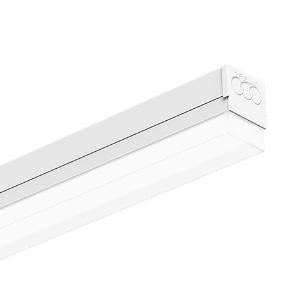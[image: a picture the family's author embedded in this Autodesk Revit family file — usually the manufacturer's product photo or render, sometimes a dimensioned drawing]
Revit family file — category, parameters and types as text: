
# Revit family: 3f_filippi_-_3f_zeta_dr_3f_filippi_-_10971_-_3f_zeta_dr_2x18_led_dali_l1194
name_source: partatom
category: Lighting Fixtures
units: mm (PartAtom-declared; Revit-internal decimal feet)

## family parameters
Cut with Voids When Loaded = No
Host = Face
Light Source = No
Part Type = Normal
Room Calculation Point = No
Round Connector Dimension = Use Diameter
Shared = No

## types (1)
- 3F Filippi - 3F Zeta DR (1 x LED, 4851 lm, 40 W, 4000 K)
    Apparent Load = 40 VA
    Approval mark = CE
    CIE Flux Codes = 41 72 91 86 100
    Color Rendering = 80
    Color Temperature = 4000 K
    Control Gear = Electronic transformer
    Default Elevation = 1800 mm
    Description = ILLUMINOTECHNICAL
Luminous efficiency 100% (DLOR 86%, ULOR 14%).
Initial luminous flux of the luminaire 4851 lm.
Diffused symmetric distribution.
Installation Interdistance Transv.D = 1.31 x hu - Long.D = 1.25 x hu.
Tabular UGR (CIE 117 - 4H-8H; S=0.25H; 70/50/20): RUG 25.5 - 24.1.
Beam angle: 136° - 112°.
Luminous efficacy 121 lm/W.
Lifetime (L93/B10): 30000 h. (tq+25°C)
Lifetime (L90/B10): 50000 h. (tq+25°C)
Lifetime (L85/B10): 80000 h. (tq+25°C)
Lifetime (L80/B10): 100000 h. (tq+25°C)
Sudden decreased luminous flux after 50000 hours: 0% (C0).
Photobiological safety in compliance with IEC/TR 62778: RG0 risk exempt, (IEC 62471).
In compliance with IEC/EN 62722-2-1 - IEC/EN 62717 standards.

SOURCE
2 linear LED modules 18W/840.
Energy efficiency class (UE 2019/2020 - UE 2019/2015): D.
CIE 13.3 Colour rendering index: CRI >80 (R9 <50%).
IES TM-30 Fidelity Index: Rf = 84 Rg = 95.
CCT nominal colour temperature 4000 K.
Colour initial tolerance (MacAdam): SDCM 3.

MECHANICAL
Housing in hot-galvanised steel, painted in white polyester, obtained through rolling process.
Light unit in hot-galvanised steel, painted in white polyester base with fixing springs and retractable safety hooks in stainless steel.
Rectangular screen in self-extinguishing polycarbonate, UV stabilised, opal, with smooth outer surface.
End caps in white polycarbonate.
Pair of stainless steel sliding brackets with sliding block screws.
Luminaire with limited surface temperature. - D - (EN 60598-2-24)
Dimensions: 1194x62 mm, height 81 mm. Weight 3.5 kg.
IP40 protection degree.
Mechanical strength to impacts IK06 (1 joule).
Glow-wire test resistance 850°C.

ELECTRICAL
Halogen Free DALI-2 DATI (Parts 251, 252, 253), PUSH-DIM, electronic wiring 230V-50/60Hz, power factor 0.95 at full load, THD <25%, constant output current, SELV, class I, 1 driver, 1 DALI addresse.
Power of the luminaire 40 W.
ENEC - CE.
SAFE FLICKER: PstLM=<1 and SVM=<0.4 (IEC TR 61547-1 and IEC TR 63158), to ensure a more comfortable and safe light.
Luminaire compliant with EN 60598-2-22 for power supply from a centralised emergency system CPSS (Central Power Supply System), not incorporated in the luminaire - high risk areas excluded. The default power and flux are 100% in AC and 15% in DC.
Ambient temperature from 0°C to +25°C.
Temperature class T6 max 85°C.
Relative humidity UR: <85%.

INSTALLATION
Ceiling / Suspended / Wall.
All accessories dedicated to this product are available on the Catalog and on our website www.3F-Filippi.com.

APPLICATIONS
Suitable product for food production plants (HACCP), IFS (Food Version 6), BRC (GSFS Food Version 7).
In commercial environments, exhibition areas, shops and stores.

LIGHT MANAGEMENT
Recommended minimum setting: 10%.
The luminaire, equipped with (DALI-2 DATI) driver, can be controlled manually with 3F Easy Dim technology or automatically/manually with wired or wireless DALI/D2D control systems.
The D2D driver guarantees interoperability with other devices with the same certification by making the following information available:
Device Data (Part 251), Energy Report (Part 252), Diagnosis & Maintenance (Part 253).
In electrical systems without a regulation system (manual or automatic) and DALI bus, a suitable jumper must be made on the DA-DA terminals of the appliance.

WARNING
Luminaire designed for disposal/recycling at end-of-life.
Replaceable (LED only) light source by a professional. Replaceable control gear by a professional.
    Height = 81 mm
    Lamp = 1 x LED
    Lamp Light Flux = 4851 lm
    Lamp Power = 40 W
    Lamp count = 1
    Length = 1194 mm
    Lifetime = 50000 h
    Luminous efficacy = 121 lm/W
    Manufacturer = 3F Filippi
    ModVariant = No
    Model = 3F Filippi - 10971 - 3F Zeta DR 2x18 LED DALI L1194
    Mounting Place = Ceiling
    Mounting Type = Pendant
    Number of Poles = 1
    OnlyDefault = Yes
    Power Factor = 1
    Product Name = 3F Filippi - 3F Zeta DR
    Product group = pendant luminaire
    ProductGroupID = 9
    Protection Class = Protection class I
    Protection Degree = IP 40
    RLX_Detail_Level = 1
    RLX_Emergency_Light_Flux = 0 lm
    RLX_Emergency_Type = 0
    RLX_Emergency_Type_DB = No
    RlxData = <blob elided: 35289 chars, md5=2ff1a5d9>
    Socket = socket
    Standby Power = 0 W
    System Light Flux = 4851 lm
    System Power = 40 W
    Type Comments = Product without accessories
    Type Image = 3ffilippi_3f_zeta_dr.jpg
    URL = http://relux.com
    VarID = ---
    Voltage = 0 V
    Weight = 0.00 kg
    Width = 62 mm  [stored 0.203412 ft]

note: [stored X ft] marks values corroborated as IEEE doubles in the binary element streams (Revit-internal decimal feet)

## geometry (parser evidence)
native form markers: Blend x4, Sweep x11
no freeform markers — native parametric forms only
